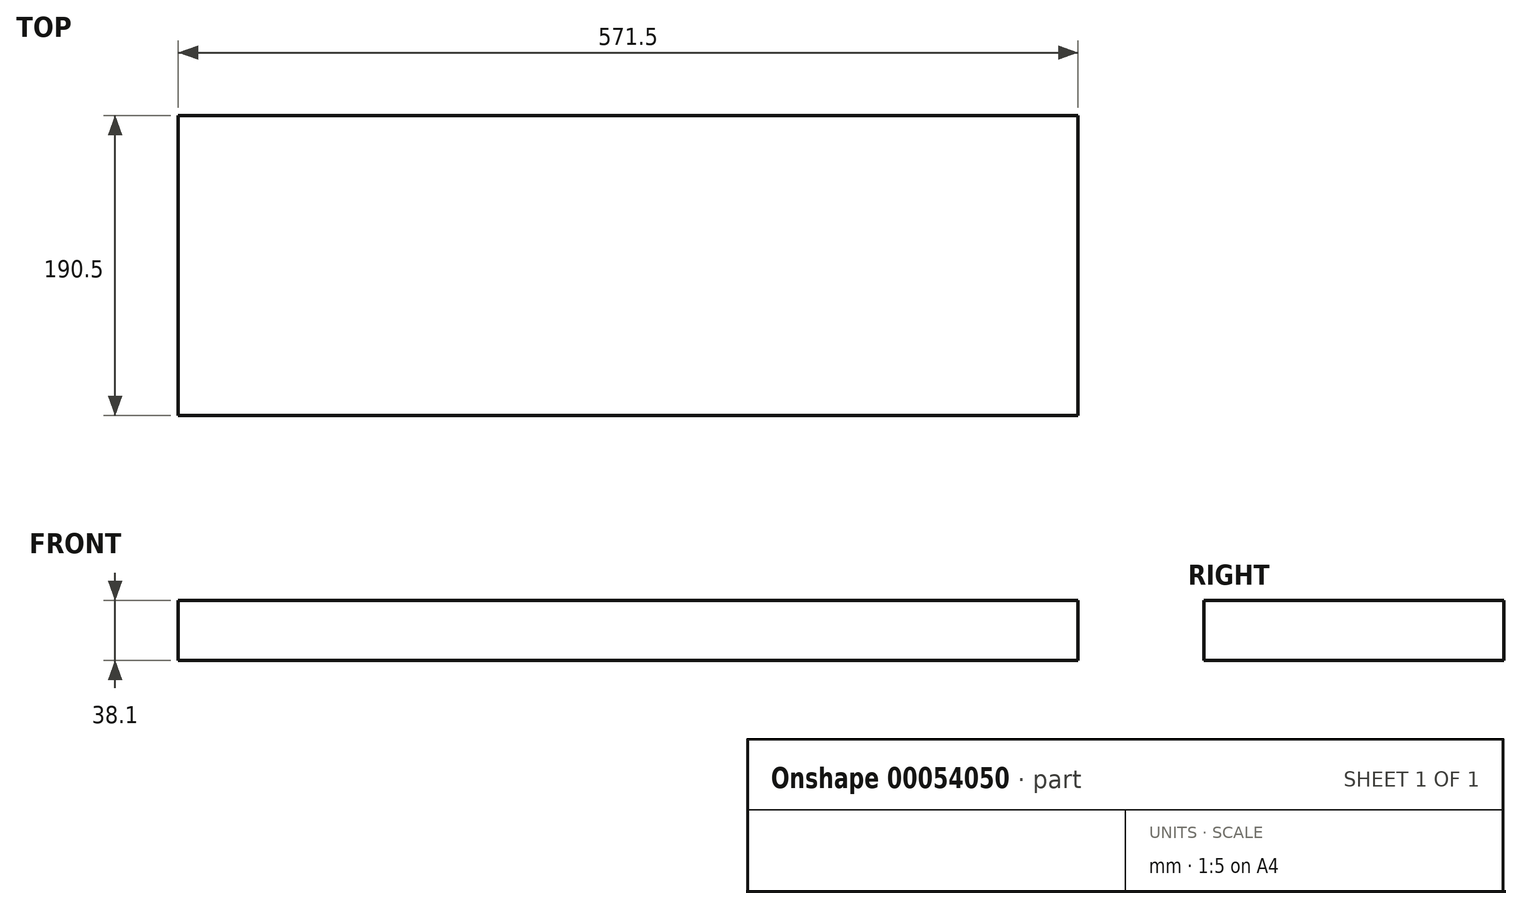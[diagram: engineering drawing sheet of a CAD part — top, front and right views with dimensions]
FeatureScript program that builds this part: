
annotation { "Feature Type Name" : "Feature", "Feature Type Description" : "" }
export const myFeature = defineFeature(function(context is Context, id is Id, definition is map)
    precondition{}
    {
        {
            var Q0;
            Q0=qCreatedBy(makeId("Right.planeOp"),FACE);
            var sketch = newSketch(context, id + "F0", { "sketchPlane" : qUnion([Q0])});
            skLineSegment(sketch, "E0.bottom", {"start": v(4.12, -3.25) * mm, "end": v(194.62, -3.25) * mm});
            skLineSegment(sketch, "E0.top", {"start": v(4.12, 34.85) * mm, "end": v(194.62, 34.85) * mm});
            skLineSegment(sketch, "E0.left", {"start": v(4.12, -3.25) * mm, "end": v(4.12, 34.85) * mm});
            skLineSegment(sketch, "E0.right", {"start": v(194.62, -3.25) * mm, "end": v(194.62, 34.85) * mm});
            skSolve(sketch);
        }
        {
            var Q0;
            Q0=makeQuery(id+"F0.imprint","IMPRINT",FACE,{"disambiguationData":[TD([[makeQuery(id+"F0.imprint","IMPRINT",EDGE,{"derivedFrom":sQuery(id+"F0.wireOp",EDGE,"E0.bottom")}),1.0]])]});
            extrude(context, id + "F1", {"entities" : qUnion([Q0]), "depth" : 571.5 * mm});
        }
    });
